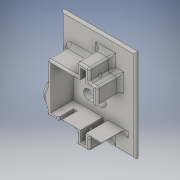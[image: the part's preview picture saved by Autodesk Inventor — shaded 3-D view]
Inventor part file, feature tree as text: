
AUTODESK INVENTOR PART (.ipt)
format: ipt  version: 2016 (Build 200138000, 138)  size: 626,176 bytes
history: native  units: in
note: dims shown in document units (in); Inventor stores cm internally (conversion verified against a paired STEP export)
features: sketch x10, other x3
ambient origin geometry x8: Origin, YZ Plane, XZ Plane, XY Plane, X Axis, Y Axis, Z Axis, Center Point
bodies: Solid1 (feature_tree)
feature tree (13):
  other  "sole_v1.ipt"
  other  "Solid1::sole_v1.ipt"
  other  "TaggingFeature1"
  sketch  "Sketch1"  dims[d0=0.3937in]
  sketch  "Sketch12"
  sketch  "Sketch14"
  sketch  "Sketch17"
  sketch  "Sketch18"
  sketch  "Sketch20"
  sketch  "Sketch21"
  sketch  "Sketch22"
  sketch  "Sketch23"
  sketch  "Sketch24"
